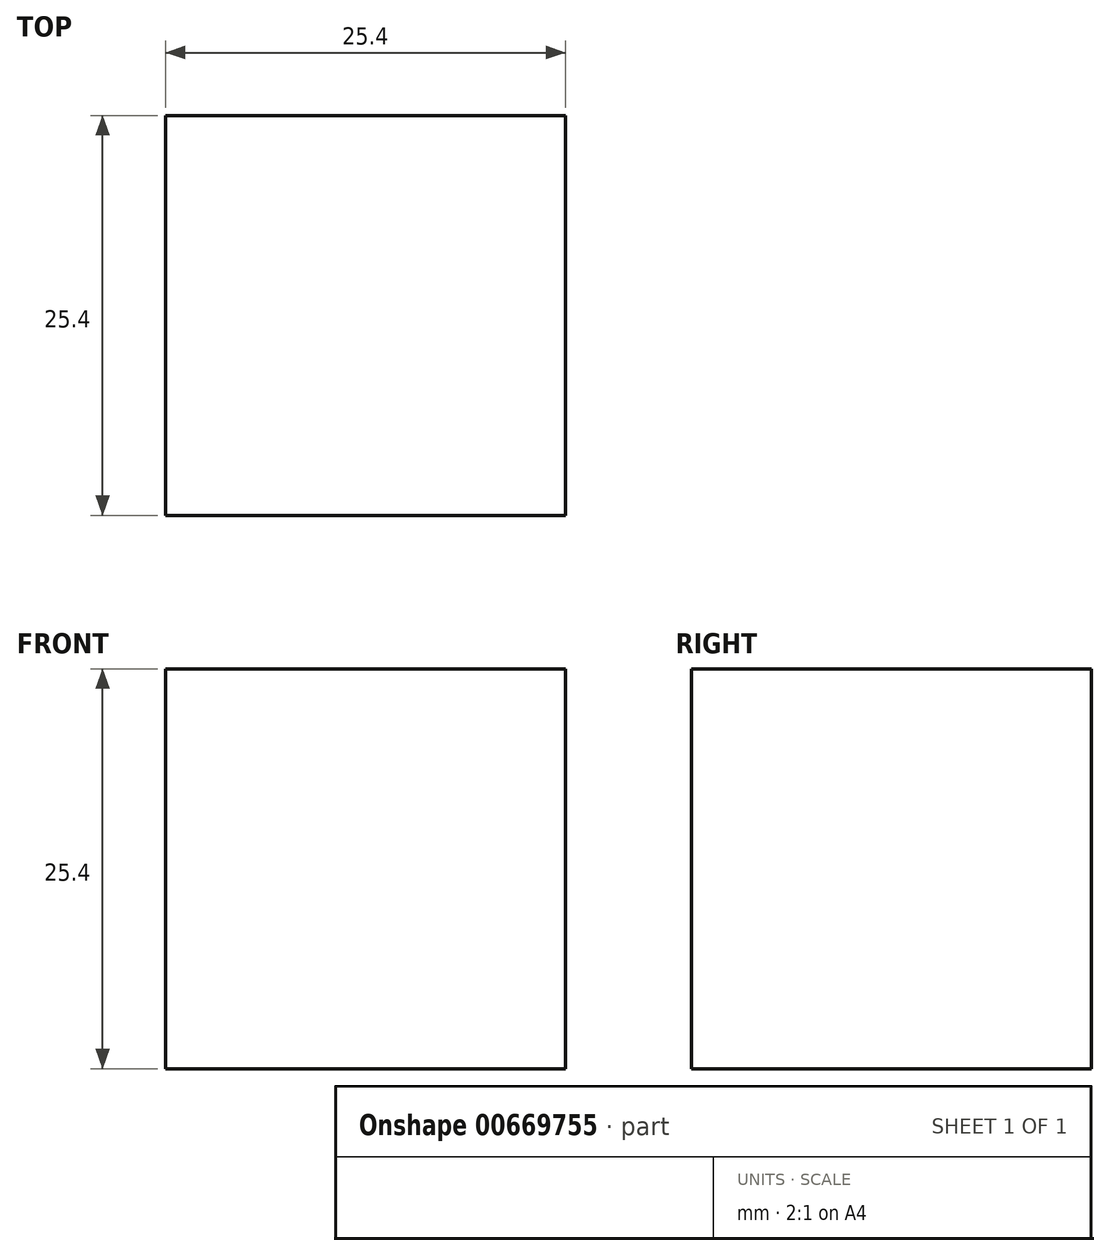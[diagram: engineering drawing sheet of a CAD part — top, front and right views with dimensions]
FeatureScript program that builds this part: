
annotation { "Feature Type Name" : "Feature", "Feature Type Description" : "" }
export const myFeature = defineFeature(function(context is Context, id is Id, definition is map)
    precondition{}
    {
        {
            var Q0;
            Q0=qCreatedBy(makeId("Front.planeOp"),FACE);
            var sketch = newSketch(context, id + "F0", { "sketchPlane" : qUnion([Q0])});
            skLineSegment(sketch, "E0", {"start": v(0, 0) * mm, "end": v(25.4, 0) * mm});
            skLineSegment(sketch, "E1", {"start": v(25.4, 0) * mm, "end": v(25.4, 25.4) * mm});
            skLineSegment(sketch, "E2", {"start": v(25.4, 25.4) * mm, "end": v(0, 25.4) * mm});
            skLineSegment(sketch, "E3", {"start": v(0, 25.4) * mm, "end": v(0, 0) * mm});
            skSolve(sketch);
        }
        {
            var Q0;
            Q0=makeQuery(id+"F0.imprint","IMPRINT",FACE,{"disambiguationData":[TD([[makeQuery(id+"F0.imprint","IMPRINT",EDGE,{"derivedFrom":sQuery(id+"F0.wireOp",EDGE,"E0")}),1.0]])]});
            extrude(context, id + "F1", {"entities" : qUnion([Q0]), "depth" : 25.4 * mm, "offsetDistance" : 25.4 * mm});
        }
    });
